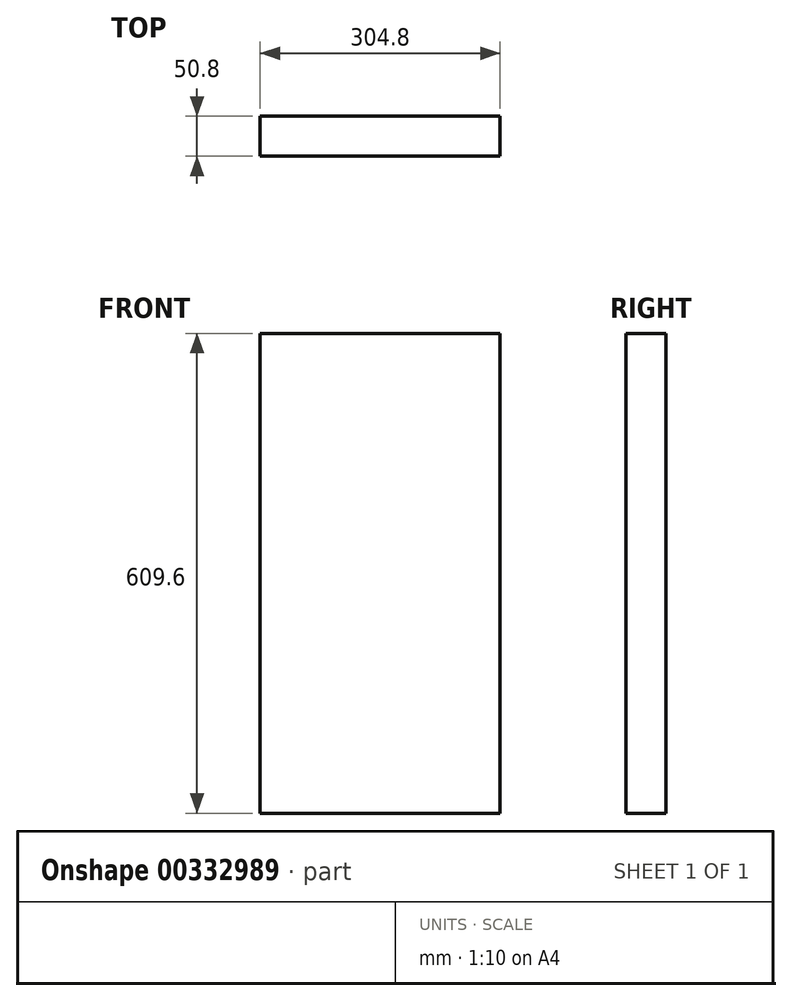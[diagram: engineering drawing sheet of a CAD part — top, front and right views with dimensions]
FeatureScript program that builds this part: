
annotation { "Feature Type Name" : "Feature", "Feature Type Description" : "" }
export const myFeature = defineFeature(function(context is Context, id is Id, definition is map)
    precondition{}
    {
        {
            var Q0;
            Q0=qCreatedBy(makeId("Front.planeOp"),FACE);
            var sketch = newSketch(context, id + "F0", { "sketchPlane" : qUnion([Q0])});
            skLineSegment(sketch, "E0.bottom", {"start": v(-144.18, 437.9) * mm, "end": v(160.62, 437.9) * mm});
            skLineSegment(sketch, "E0.top", {"start": v(-144.18, -171.7) * mm, "end": v(160.62, -171.7) * mm});
            skLineSegment(sketch, "E0.left", {"start": v(-144.18, 437.9) * mm, "end": v(-144.18, -171.7) * mm});
            skLineSegment(sketch, "E0.right", {"start": v(160.62, 437.9) * mm, "end": v(160.62, -171.7) * mm});
            skSolve(sketch);
        }
        {
            var Q0;
            Q0=makeQuery(id+"F0.imprint","IMPRINT",FACE,{"disambiguationData":[TD([[makeQuery(id+"F0.imprint","IMPRINT",EDGE,{"derivedFrom":sQuery(id+"F0.wireOp",EDGE,"E0.bottom")}),-1.0]])]});
            extrude(context, id + "F1", {"entities" : qUnion([Q0]), "depth" : 50.8 * mm});
        }
    });
